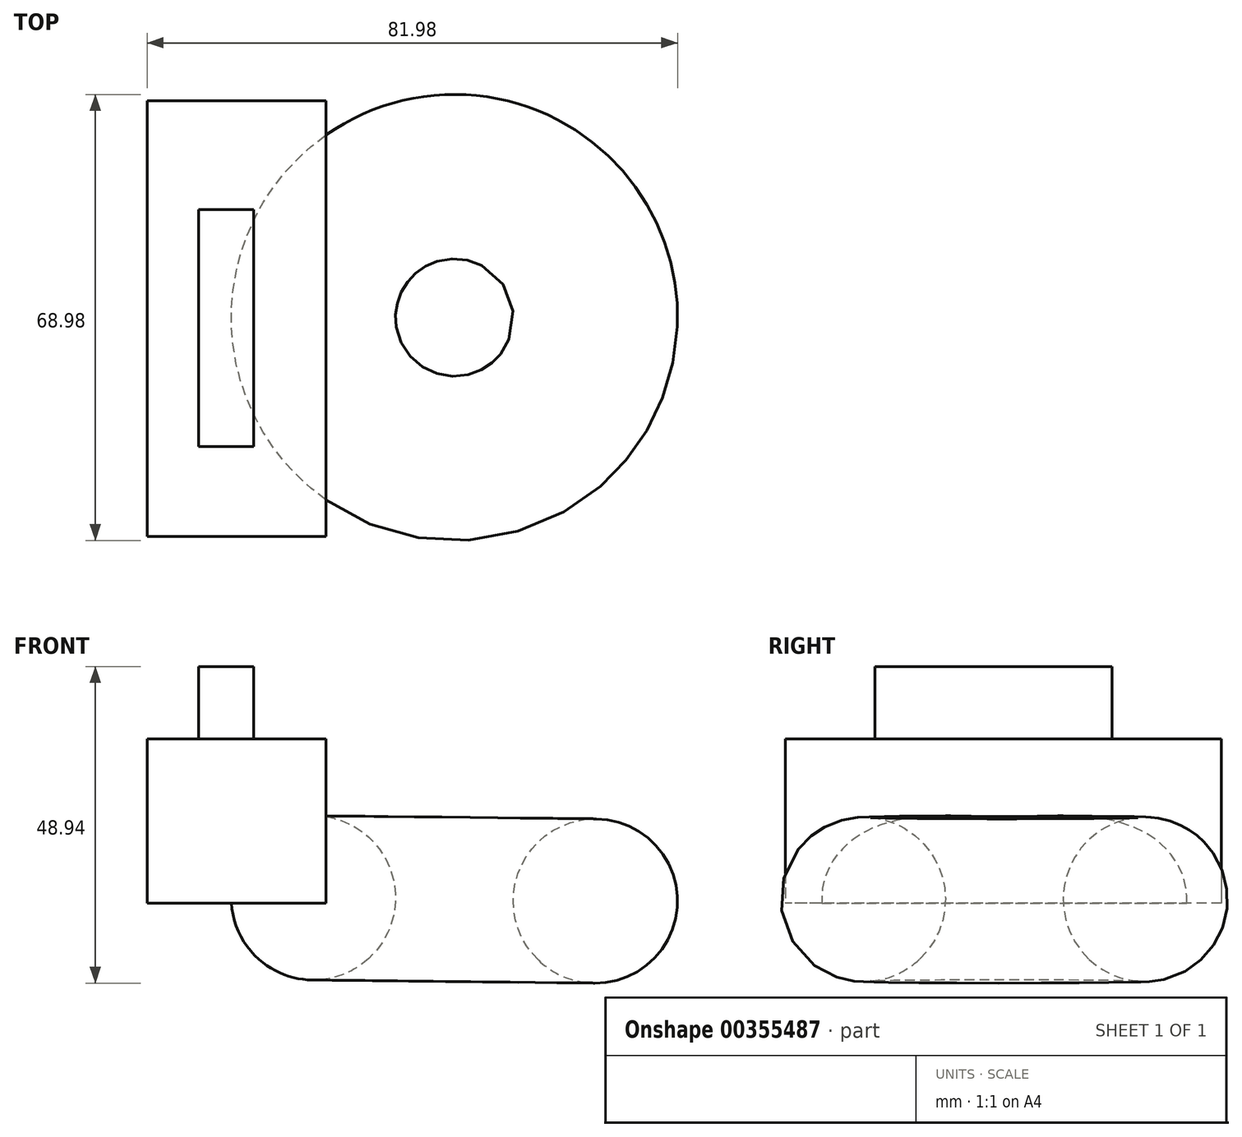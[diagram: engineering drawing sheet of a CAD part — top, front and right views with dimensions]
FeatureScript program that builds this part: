
annotation { "Feature Type Name" : "Feature", "Feature Type Description" : "" }
export const myFeature = defineFeature(function(context is Context, id is Id, definition is map)
    precondition{}
    {
        {
            var Q0;
            Q0=qCreatedBy(makeId("Front.planeOp"),FACE);
            var sketch = newSketch(context, id + "F0", { "sketchPlane" : qUnion([Q0])});
            skCircle(sketch, "E0", {"center": v(0.03, 0.34) * mm, "radius": 12.7 * mm});
            skSolve(sketch);
        }
        {
            var Q0;
            Q0=qCreatedBy(makeId("Front.planeOp"),FACE);
            var sketch = newSketch(context, id + "F1", { "sketchPlane" : qUnion([Q0])});
            skLineSegment(sketch, "E1", {"start": v(-21.76, 0) * mm, "end": v(-22.34, -52.96) * mm});
            skSolve(sketch);
        }
        {
            var Q0;
            Q0=makeQuery(id+"F0.imprint","IMPRINT",FACE,{"disambiguationData":[TD([[makeQuery(id+"F0.imprint","IMPRINT",EDGE,{"derivedFrom":sQuery(id+"F0.wireOp",EDGE,"E0")}),1.0]])]});
            var Q1;
            Q1=sQuery(id+"F1.wireOp",EDGE,"E1");
            revolve(context, id + "F2", {"entities" : qUnion([Q0]), "axis" : qUnion([Q1]), "revolveType" : RevolveType.FULL});
        }
        {
            var Q0;
            Q0=qCreatedBy(makeId("Top.planeOp"),FACE);
            var sketch = newSketch(context, id + "F3", { "sketchPlane" : qUnion([Q0])});
            skLineSegment(sketch, "E2.bottom", {"start": v(-41.6, 33.53) * mm, "end": v(-69.25, 33.53) * mm});
            skLineSegment(sketch, "E2.top", {"start": v(-41.6, -33.85) * mm, "end": v(-69.25, -33.85) * mm});
            skLineSegment(sketch, "E2.left", {"start": v(-41.6, 33.53) * mm, "end": v(-41.6, -33.85) * mm});
            skLineSegment(sketch, "E2.right", {"start": v(-69.25, 33.53) * mm, "end": v(-69.25, -33.85) * mm});
            skSolve(sketch);
        }
        {
            var Q0;
            Q0=makeQuery(id+"F3.imprint","IMPRINT",FACE,{"disambiguationData":[TD([[makeQuery(id+"F3.imprint","IMPRINT",EDGE,{"derivedFrom":sQuery(id+"F3.wireOp",EDGE,"E2.bottom")}),1.0]])]});
            extrude(context, id + "F4", {"entities" : qUnion([Q0]), "operationType" : NewBodyOperationType.ADD, "depth" : 25.4 * mm});
        }
        {
            var Q0;
            Q0=makeQuery(id+"F4.opExtrude","CAP_FACE",FACE,{"disambiguationData":[OSD([sQuery(id+"F3.wireOp",EDGE,"E2.bottom"),sQuery(id+"F3.wireOp",EDGE,"E2.top"),sQuery(id+"F3.wireOp",EDGE,"E2.left"),sQuery(id+"F3.wireOp",EDGE,"E2.right")])],"isStart":false});
            var sketch = newSketch(context, id + "F5", { "sketchPlane" : qUnion([Q0])});
            skLineSegment(sketch, "E3.bottom", {"start": v(-52.76, 16.66) * mm, "end": v(-61.28, 16.66) * mm});
            skLineSegment(sketch, "E3.top", {"start": v(-52.76, -19.96) * mm, "end": v(-61.28, -19.96) * mm});
            skLineSegment(sketch, "E3.left", {"start": v(-52.76, 16.66) * mm, "end": v(-52.76, -19.96) * mm});
            skLineSegment(sketch, "E3.right", {"start": v(-61.28, 16.66) * mm, "end": v(-61.28, -19.96) * mm});
            skSolve(sketch);
        }
        {
            var Q0;
            Q0=makeQuery(id+"F5.imprint","IMPRINT",FACE,{"disambiguationData":[TD([[makeQuery(id+"F5.imprint","IMPRINT",EDGE,{"derivedFrom":sQuery(id+"F5.wireOp",EDGE,"E3.bottom")}),1.0]])]});
            extrude(context, id + "F6", {"entities" : qUnion([Q0]), "operationType" : NewBodyOperationType.ADD, "depth" : 11.18 * mm});
        }
    });
